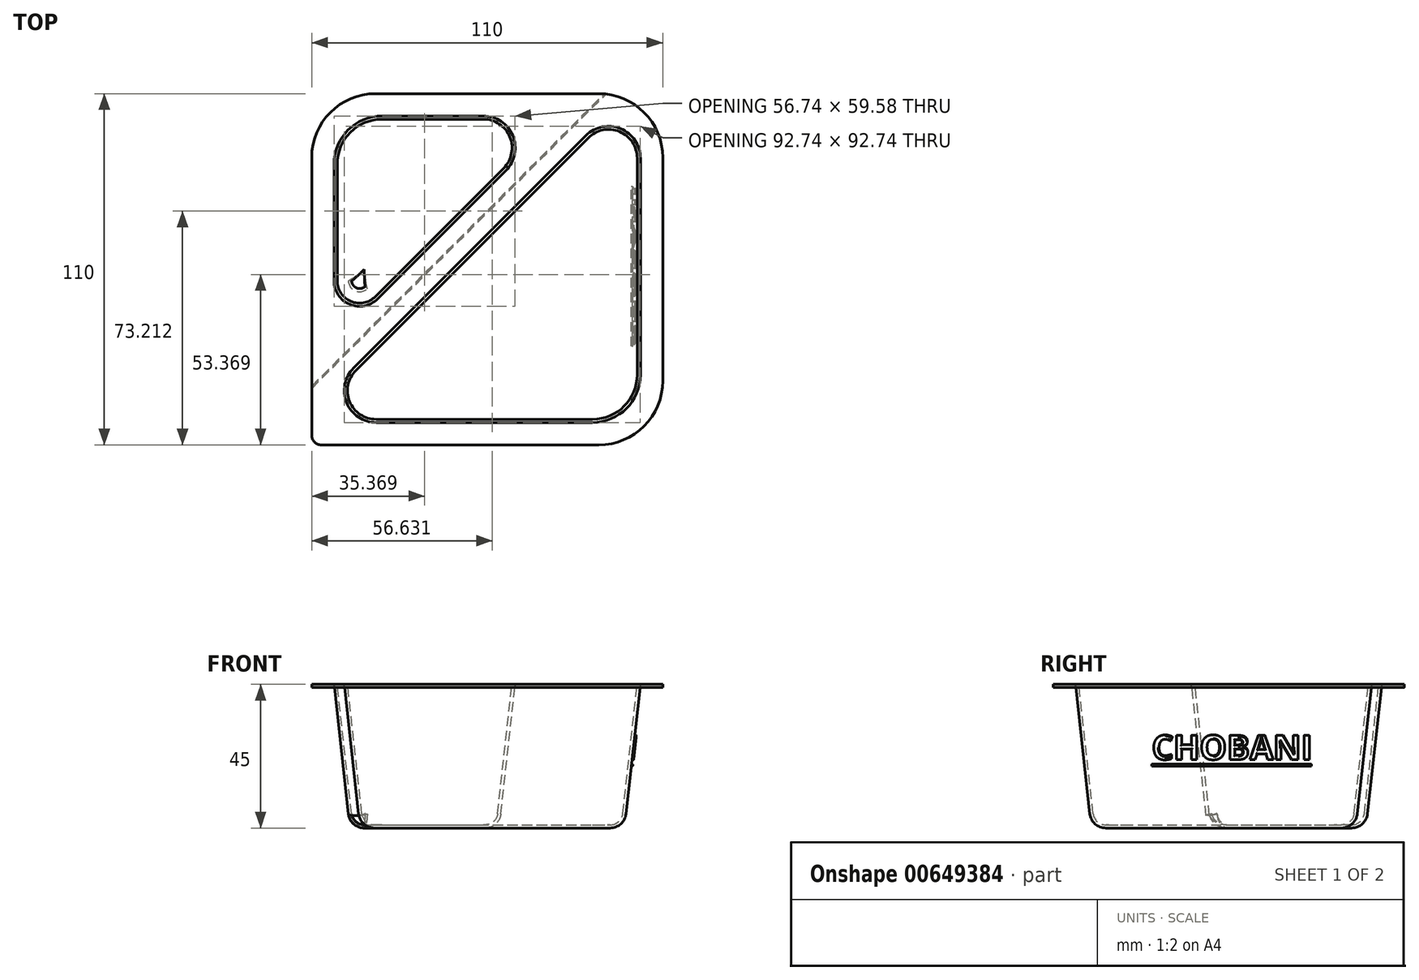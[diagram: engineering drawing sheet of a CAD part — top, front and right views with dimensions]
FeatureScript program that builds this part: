
annotation { "Feature Type Name" : "Feature", "Feature Type Description" : "" }
export const myFeature = defineFeature(function(context is Context, id is Id, definition is map)
    precondition{}
    {
        {
            var Q0;
            Q0=qCreatedBy(makeId("Top.planeOp"),FACE);
            cPlane(context, id + "F0", {"entities" : qUnion([Q0]), "cplaneType" : CPlaneType.OFFSET, "offset" : 45 * mm, "width" : 150 * mm, "height" : 150 * mm});
        }
        {
            var Q0;
            Q0=qCreatedBy(id+"F0.planeOp",FACE);
            var sketch = newSketch(context, id + "F1", { "sketchPlane" : qUnion([Q0])});
            skLineSegment(sketch, "E0.bottom", {"start": v(-52, -55) * mm, "end": v(35, -55) * mm});
            skLineSegment(sketch, "E0.top", {"start": v(-35, 55) * mm, "end": v(35, 55) * mm});
            skLineSegment(sketch, "E0.left", {"start": v(-55, -52) * mm, "end": v(-55, 35) * mm});
            skLineSegment(sketch, "E0.right", {"start": v(55, -35) * mm, "end": v(55, 35) * mm});
            skPoint(sketch, "E0.middle", {"position": v(0, 0) * mm});
            skPoint(sketch, "E1.visualSharp", {"position": v(-55, 55) * mm});
            skArc(sketch, "E1.filletArc", {"start": v(-35, 55) * mm, "mid": v(-49.14, 49.14) * mm, "end": v(-55, 35) * mm});
            skPoint(sketch, "E2.visualSharp", {"position": v(55, 55) * mm});
            skArc(sketch, "E2.filletArc", {"start": v(55, 35) * mm, "mid": v(49.14, 49.14) * mm, "end": v(35, 55) * mm});
            skPoint(sketch, "E3.visualSharp", {"position": v(55, -55) * mm});
            skArc(sketch, "E3.filletArc", {"start": v(35, -55) * mm, "mid": v(49.14, -49.14) * mm, "end": v(55, -35) * mm});
            skPoint(sketch, "E4.visualSharp", {"position": v(-55, -55) * mm});
            skArc(sketch, "E4.filletArc", {"start": v(-55, -52) * mm, "mid": v(-54.12, -54.12) * mm, "end": v(-52, -55) * mm});
            skSolve(sketch);
        }
        {
            var Q0;
            Q0=makeQuery(id+"F1.imprint","IMPRINT",FACE,{"disambiguationData":[TD([[makeQuery(id+"F1.imprint","IMPRINT",EDGE,{"derivedFrom":sQuery(id+"F1.wireOp",EDGE,"E0.bottom")}),1.0]])]});
            extrude(context, id + "F2", {"entities" : qUnion([Q0]), "oppositeDirection" : true, "depth" : 1 * mm, "offsetDistance" : 25 * mm});
        }
        {
            var Q0;
            Q0=makeQuery(id+"F2.opExtrude","CAP_FACE",FACE,{"disambiguationData":[OSD([sQuery(id+"F1.wireOp",EDGE,"E0.bottom"),sQuery(id+"F1.wireOp",EDGE,"E0.top"),sQuery(id+"F1.wireOp",EDGE,"E0.left"),sQuery(id+"F1.wireOp",EDGE,"E0.right"),sQuery(id+"F1.wireOp",EDGE,"E1.filletArc"),sQuery(id+"F1.wireOp",EDGE,"E2.filletArc"),sQuery(id+"F1.wireOp",EDGE,"E3.filletArc"),sQuery(id+"F1.wireOp",EDGE,"E4.filletArc")])],"isStart":true});
            var sketch = newSketch(context, id + "F3", { "sketchPlane" : qUnion([Q0])});
            skLineSegment(sketch, "E5", {"start": v(-55, -37) * mm, "end": v(48.56, 66.56) * mm, "construction": true});
            skLineSegment(sketch, "E6", {"start": v(-48, -3.62) * mm, "end": v(-48, 33) * mm});
            skLineSegment(sketch, "E7", {"start": v(-33, 48) * mm, "end": v(-1.21, 48) * mm});
            skLineSegment(sketch, "E8", {"start": v(5.86, 30.93) * mm, "end": v(-34.34, -9.27) * mm});
            skPoint(sketch, "E9.visualSharp", {"position": v(22.93, 48) * mm});
            skArc(sketch, "E9.filletArc", {"start": v(5.86, 30.93) * mm, "mid": v(8.03, 41.83) * mm, "end": v(-1.21, 48) * mm});
            skPoint(sketch, "E10.visualSharp", {"position": v(-48, -22.93) * mm});
            skArc(sketch, "E10.filletArc", {"start": v(-48, -3.62) * mm, "mid": v(-43.06, -11) * mm, "end": v(-34.34, -9.27) * mm});
            skPoint(sketch, "E11.visualSharp", {"position": v(-48, 48) * mm});
            skArc(sketch, "E11.filletArc", {"start": v(-33, 48) * mm, "mid": v(-43.6, 43.6) * mm, "end": v(-48, 33) * mm});
            skLineSegment(sketch, "E12", {"start": v(-34.79, -48) * mm, "end": v(33, -48) * mm});
            skLineSegment(sketch, "E13", {"start": v(48, -33) * mm, "end": v(48, 34.79) * mm});
            skLineSegment(sketch, "E14", {"start": v(30.93, 41.86) * mm, "end": v(-41.86, -30.93) * mm});
            skPoint(sketch, "E15.visualSharp", {"position": v(48, 58.93) * mm});
            skArc(sketch, "E15.filletArc", {"start": v(48, 34.79) * mm, "mid": v(41.83, 44.03) * mm, "end": v(30.93, 41.86) * mm});
            skPoint(sketch, "E16.visualSharp", {"position": v(-58.93, -48) * mm});
            skArc(sketch, "E16.filletArc", {"start": v(-41.86, -30.93) * mm, "mid": v(-44.03, -41.83) * mm, "end": v(-34.79, -48) * mm});
            skPoint(sketch, "E17.visualSharp", {"position": v(48, -48) * mm});
            skArc(sketch, "E17.filletArc", {"start": v(33, -48) * mm, "mid": v(43.6, -43.6) * mm, "end": v(48, -33) * mm});
            skSolve(sketch);
        }
        {
            var Q0;
            Q0=qCreatedBy(makeId("Top.planeOp"),FACE);
            var sketch = newSketch(context, id + "F4", { "sketchPlane" : qUnion([Q0])});
            skArc(sketch, "E18.0", {"start": v(-43, -3.62) * mm, "mid": v(-41.15, -6.39) * mm, "end": v(-37.88, -5.74) * mm});
            skArc(sketch, "E18.1", {"start": v(-33, 43) * mm, "mid": v(-40.07, 40.07) * mm, "end": v(-43, 33) * mm});
            skLineSegment(sketch, "E18.2", {"start": v(-33, 43) * mm, "end": v(-1.21, 43) * mm});
            skLineSegment(sketch, "E18.3", {"start": v(-43, -3.62) * mm, "end": v(-43, 33) * mm});
            skArc(sketch, "E18.4", {"start": v(2.32, 34.46) * mm, "mid": v(3.4, 39.91) * mm, "end": v(-1.21, 43) * mm});
            skLineSegment(sketch, "E18.5", {"start": v(2.32, 34.46) * mm, "end": v(-37.88, -5.74) * mm});
            skLineSegment(sketch, "E19.0", {"start": v(34.46, 38.32) * mm, "end": v(-38.32, -34.46) * mm});
            skLineSegment(sketch, "E19.1", {"start": v(-34.79, -43) * mm, "end": v(33, -43) * mm});
            skArc(sketch, "E19.2", {"start": v(33, -43) * mm, "mid": v(40.07, -40.07) * mm, "end": v(43, -33) * mm});
            skArc(sketch, "E19.3", {"start": v(-38.32, -34.46) * mm, "mid": v(-39.4, -39.91) * mm, "end": v(-34.79, -43) * mm});
            skLineSegment(sketch, "E19.4", {"start": v(43, -33) * mm, "end": v(43, 34.79) * mm});
            skArc(sketch, "E19.5", {"start": v(43, 34.79) * mm, "mid": v(39.91, 39.4) * mm, "end": v(34.46, 38.32) * mm});
            skSolve(sketch);
        }
        {
            var Q0;
            Q0=makeQuery(id+"F3.imprint","IMPRINT",FACE,{"disambiguationData":[TD([[makeQuery(id+"F3.imprint","IMPRINT",EDGE,{"derivedFrom":sQuery(id+"F3.wireOp",EDGE,"E6")}),-1.0]])]});
            var Q1;
            Q1=makeQuery(id+"F3.imprint","IMPRINT",FACE,{"disambiguationData":[TD([[makeQuery(id+"F3.imprint","IMPRINT",EDGE,{"derivedFrom":sQuery(id+"F3.wireOp",EDGE,"E12")}),1.0]])]});
            extrude(context, id + "F5", {"entities" : qUnion([Q0, Q1]), "operationType" : NewBodyOperationType.REMOVE, "oppositeDirection" : true, "depth" : 25 * mm, "offsetDistance" : 25 * mm});
        }
        {
            var Q0;
            Q0=makeQuery(id+"F3.imprint","IMPRINT",FACE,{"disambiguationData":[TD([[makeQuery(id+"F3.imprint","IMPRINT",EDGE,{"derivedFrom":sQuery(id+"F3.wireOp",EDGE,"E6")}),-1.0]])]});
            var Q1;
            Q1=makeQuery(id+"F4.imprint","IMPRINT",FACE,{"disambiguationData":[TD([[makeQuery(id+"F4.imprint","IMPRINT",EDGE,{"derivedFrom":sQuery(id+"F4.wireOp",EDGE,"E18.0")}),1.0]])]});
            loft(context, id + "F6", {"sheetProfilesArray" : [{ "sheetProfileEntities" : qUnion([Q0]) }, { "sheetProfileEntities" : qUnion([Q1]) }]});
        }
        {
            var Q0;
            Q0=makeQuery(id+"F3.imprint","IMPRINT",FACE,{"disambiguationData":[TD([[makeQuery(id+"F3.imprint","IMPRINT",EDGE,{"derivedFrom":sQuery(id+"F3.wireOp",EDGE,"E12")}),1.0]])]});
            var Q1;
            Q1=makeQuery(id+"F4.imprint","IMPRINT",FACE,{"disambiguationData":[TD([[makeQuery(id+"F4.imprint","IMPRINT",EDGE,{"derivedFrom":sQuery(id+"F4.wireOp",EDGE,"E19.0")}),1.0]])]});
            loft(context, id + "F7", {"sheetProfilesArray" : [{ "sheetProfileEntities" : qUnion([Q0]) }, { "sheetProfileEntities" : qUnion([Q1]) }]});
        }
        {
            var Q0;
            Q0=makeQuery(id+"F6.opLoft","MID_CAP_EDGE",EDGE,{"disambiguationData":[OSD([sQuery(id+"F4.wireOp",EDGE,"E18.1"),sQuery(id+"F4.wireOp",EDGE,"E18.2"),sQuery(id+"F4.wireOp",EDGE,"E18.3")])],"capPos":1.0});
            fillet(context, id + "F8", {"entities" : qUnion([Q0]), "radius" : 5 * mm, "tangentPropagation" : true, "allowEdgeOverflow" : false});
        }
        {
            var Q0;
            Q0=makeQuery(id+"F6.opLoft","CAP_FACE",FACE,{"disambiguationData":[OSD([makeQuery(id+"F3.imprint","IMPRINT",FACE,{"disambiguationData":[TD([[makeQuery(id+"F3.imprint","IMPRINT",EDGE,{"derivedFrom":sQuery(id+"F3.wireOp",EDGE,"E6")}),-1.0]])]})])],"isStart":true});
            shell(context, id + "F9", {"entities" : qUnion([Q0]), "thickness" : 1 * mm});
        }
        {
            var Q0;
            Q0=makeQuery(id+"F7.opLoft","MID_CAP_EDGE",EDGE,{"disambiguationData":[OSD([sQuery(id+"F4.wireOp",EDGE,"E19.0"),sQuery(id+"F4.wireOp",EDGE,"E19.1"),sQuery(id+"F4.wireOp",EDGE,"E19.3")])],"capPos":1.0});
            fillet(context, id + "F10", {"entities" : qUnion([Q0]), "radius" : 5 * mm, "tangentPropagation" : true, "allowEdgeOverflow" : false});
        }
        {
            var Q0;
            Q0=makeQuery(id+"F7.opLoft","CAP_FACE",FACE,{"disambiguationData":[OSD([makeQuery(id+"F3.imprint","IMPRINT",FACE,{"disambiguationData":[TD([[makeQuery(id+"F3.imprint","IMPRINT",EDGE,{"derivedFrom":sQuery(id+"F3.wireOp",EDGE,"E12")}),1.0]])]})])],"isStart":true});
            shell(context, id + "F11", {"entities" : qUnion([Q0]), "thickness" : 1 * mm});
        }
        {
            var Q0;
            Q0=sQuery(id+"F3.wireOp",VERTEX,"E5.end");
            var Q1;
            Q1=sQuery(id+"F3.wireOp",EDGE,"E5");
            cPlane(context, id + "F12", {"entities" : qUnion([Q0, Q1]), "cplaneType" : CPlaneType.LINE_POINT, "offset" : 25 * mm, "width" : 150 * mm, "height" : 150 * mm});
        }
        {
            var Q0;
            Q0=qCreatedBy(id+"F12.planeOp",FACE);
            var sketch = newSketch(context, id + "F13", { "sketchPlane" : qUnion([Q0])});
            skLineSegment(sketch, "E20", {"start": v(12.73, 44.3) * mm, "end": v(12.98, 44) * mm});
            skLineSegment(sketch, "E21", {"start": v(12.98, 44) * mm, "end": v(12.48, 44) * mm});
            skLineSegment(sketch, "E22", {"start": v(12.48, 44) * mm, "end": v(12.73, 44.3) * mm});
            skSolve(sketch);
        }
        {
            var Q0;
            Q0=makeQuery(id+"F13.imprint","IMPRINT",FACE,{"disambiguationData":[TD([[makeQuery(id+"F13.imprint","IMPRINT",EDGE,{"derivedFrom":sQuery(id+"F13.wireOp",EDGE,"E20")}),-1.0]])]});
            extrude(context, id + "F14", {"entities" : qUnion([Q0]), "operationType" : NewBodyOperationType.REMOVE, "endBound" : BoundingType.THROUGH_ALL, "oppositeDirection" : true, "depth" : 25 * mm, "offsetDistance" : 25 * mm});
        }
        {
            var Q0;
            Q0=makeQuery(id+"F7.opLoft","SWEPT_FACE",FACE,{"disambiguationData":[OSD([sQuery(id+"F3.wireOp",EDGE,"E13"),sQuery(id+"F3.wireOp",EDGE,"E15.filletArc"),sQuery(id+"F3.wireOp",EDGE,"E17.filletArc"),sQuery(id+"F4.wireOp",EDGE,"E19.2"),sQuery(id+"F4.wireOp",EDGE,"E19.4"),sQuery(id+"F4.wireOp",EDGE,"E19.5")])]});
            var sketch = newSketch(context, id + "F15", { "sketchPlane" : qUnion([Q0])});
            skText(sketch, "E23", { "text": "CHOBANI", "fontName": "OpenSans-Bold.ttf"});
            skLineSegment(sketch, "E24.bottom", {"start": v(-24.1, 24.84) * mm, "end": v(25.9, 24.84) * mm});
            skLineSegment(sketch, "E24.top", {"start": v(-24.1, 24.34) * mm, "end": v(25.9, 24.34) * mm});
            skLineSegment(sketch, "E24.left", {"start": v(-24.1, 24.84) * mm, "end": v(-24.1, 24.34) * mm});
            skLineSegment(sketch, "E24.right", {"start": v(25.9, 24.84) * mm, "end": v(25.9, 24.34) * mm});
            const initialGuessF15  = {"E23": [-0.0241, 0.02634, 1, 0, 0.0077]};
            skSetInitialGuess(sketch, initialGuessF15);
            skSolve(sketch);
        }
        {
            var Q0;
            Q0 = qSketchRegion(id + "F15", true);
            extrude(context, id + "F16", {"entities" : qUnion([Q0]), "operationType" : NewBodyOperationType.ADD, "depth" : .5 * mm, "offsetDistance" : 25 * mm});
        }
        {
            var Q0;
            Q0=makeQuery(id+"F16.opExtrude","CAP_FACE",FACE,{"disambiguationData":[OSD([sQuery(id+"F15.wireOp",EDGE,"E23.sketch_text.stroke-0"),sQuery(id+"F15.wireOp",EDGE,"E23.sketch_text.stroke-1"),sQuery(id+"F15.wireOp",EDGE,"E23.sketch_text.stroke-2"),sQuery(id+"F15.wireOp",EDGE,"E23.sketch_text.stroke-3"),sQuery(id+"F15.wireOp",EDGE,"E23.sketch_text.stroke-4"),sQuery(id+"F15.wireOp",EDGE,"E23.sketch_text.stroke-5"),sQuery(id+"F15.wireOp",EDGE,"E23.sketch_text.stroke-6"),sQuery(id+"F15.wireOp",EDGE,"E23.sketch_text.stroke-7"),sQuery(id+"F15.wireOp",EDGE,"E23.sketch_text.stroke-8"),sQuery(id+"F15.wireOp",EDGE,"E23.sketch_text.stroke-9"),sQuery(id+"F15.wireOp",EDGE,"E23.sketch_text.stroke-10"),sQuery(id+"F15.wireOp",EDGE,"E23.sketch_text.stroke-11"),sQuery(id+"F15.wireOp",EDGE,"E23.sketch_text.stroke-12"),sQuery(id+"F15.wireOp",EDGE,"E23.sketch_text.stroke-13"),sQuery(id+"F15.wireOp",EDGE,"E23.sketch_text.stroke-14")])],"isStart":false});
            var Q1;
            Q1=makeQuery(id+"F16.opExtrude","CAP_FACE",FACE,{"disambiguationData":[OSD([sQuery(id+"F15.wireOp",EDGE,"E23.sketch_text.stroke-15"),sQuery(id+"F15.wireOp",EDGE,"E23.sketch_text.stroke-16"),sQuery(id+"F15.wireOp",EDGE,"E23.sketch_text.stroke-17"),sQuery(id+"F15.wireOp",EDGE,"E23.sketch_text.stroke-18"),sQuery(id+"F15.wireOp",EDGE,"E23.sketch_text.stroke-19"),sQuery(id+"F15.wireOp",EDGE,"E23.sketch_text.stroke-20"),sQuery(id+"F15.wireOp",EDGE,"E23.sketch_text.stroke-21"),sQuery(id+"F15.wireOp",EDGE,"E23.sketch_text.stroke-22"),sQuery(id+"F15.wireOp",EDGE,"E23.sketch_text.stroke-23"),sQuery(id+"F15.wireOp",EDGE,"E23.sketch_text.stroke-24"),sQuery(id+"F15.wireOp",EDGE,"E23.sketch_text.stroke-25"),sQuery(id+"F15.wireOp",EDGE,"E23.sketch_text.stroke-26")])],"isStart":false});
            var Q2;
            Q2=makeQuery(id+"F16.opExtrude","CAP_FACE",FACE,{"disambiguationData":[OSD([sQuery(id+"F15.wireOp",EDGE,"E23.sketch_text.stroke-27"),sQuery(id+"F15.wireOp",EDGE,"E23.sketch_text.stroke-28"),sQuery(id+"F15.wireOp",EDGE,"E23.sketch_text.stroke-29"),sQuery(id+"F15.wireOp",EDGE,"E23.sketch_text.stroke-30"),sQuery(id+"F15.wireOp",EDGE,"E23.sketch_text.stroke-31"),sQuery(id+"F15.wireOp",EDGE,"E23.sketch_text.stroke-32"),sQuery(id+"F15.wireOp",EDGE,"E23.sketch_text.stroke-33"),sQuery(id+"F15.wireOp",EDGE,"E23.sketch_text.stroke-34"),sQuery(id+"F15.wireOp",EDGE,"E23.sketch_text.stroke-35"),sQuery(id+"F15.wireOp",EDGE,"E23.sketch_text.stroke-36"),sQuery(id+"F15.wireOp",EDGE,"E23.sketch_text.stroke-37"),sQuery(id+"F15.wireOp",EDGE,"E23.sketch_text.stroke-38"),sQuery(id+"F15.wireOp",EDGE,"E23.sketch_text.stroke-39"),sQuery(id+"F15.wireOp",EDGE,"E23.sketch_text.stroke-40")])],"isStart":false});
            var Q3;
            Q3=makeQuery(id+"F16.opExtrude","CAP_FACE",FACE,{"disambiguationData":[OSD([sQuery(id+"F15.wireOp",EDGE,"E23.sketch_text.stroke-41"),sQuery(id+"F15.wireOp",EDGE,"E23.sketch_text.stroke-42"),sQuery(id+"F15.wireOp",EDGE,"E23.sketch_text.stroke-43"),sQuery(id+"F15.wireOp",EDGE,"E23.sketch_text.stroke-44"),sQuery(id+"F15.wireOp",EDGE,"E23.sketch_text.stroke-45"),sQuery(id+"F15.wireOp",EDGE,"E23.sketch_text.stroke-46"),sQuery(id+"F15.wireOp",EDGE,"E23.sketch_text.stroke-47"),sQuery(id+"F15.wireOp",EDGE,"E23.sketch_text.stroke-48"),sQuery(id+"F15.wireOp",EDGE,"E23.sketch_text.stroke-49"),sQuery(id+"F15.wireOp",EDGE,"E23.sketch_text.stroke-50"),sQuery(id+"F15.wireOp",EDGE,"E23.sketch_text.stroke-51"),sQuery(id+"F15.wireOp",EDGE,"E23.sketch_text.stroke-52"),sQuery(id+"F15.wireOp",EDGE,"E23.sketch_text.stroke-53"),sQuery(id+"F15.wireOp",EDGE,"E23.sketch_text.stroke-54"),sQuery(id+"F15.wireOp",EDGE,"E23.sketch_text.stroke-55"),sQuery(id+"F15.wireOp",EDGE,"E23.sketch_text.stroke-56"),sQuery(id+"F15.wireOp",EDGE,"E23.sketch_text.stroke-57"),sQuery(id+"F15.wireOp",EDGE,"E23.sketch_text.stroke-58"),sQuery(id+"F15.wireOp",EDGE,"E23.sketch_text.stroke-59"),sQuery(id+"F15.wireOp",EDGE,"E23.sketch_text.stroke-60"),sQuery(id+"F15.wireOp",EDGE,"E23.sketch_text.stroke-61"),sQuery(id+"F15.wireOp",EDGE,"E23.sketch_text.stroke-62"),sQuery(id+"F15.wireOp",EDGE,"E23.sketch_text.stroke-63"),sQuery(id+"F15.wireOp",EDGE,"E23.sketch_text.stroke-64"),sQuery(id+"F15.wireOp",EDGE,"E23.sketch_text.stroke-65")])],"isStart":false});
            var Q4;
            Q4=makeQuery(id+"F16.opExtrude","CAP_FACE",FACE,{"disambiguationData":[OSD([sQuery(id+"F15.wireOp",EDGE,"E23.sketch_text.stroke-66"),sQuery(id+"F15.wireOp",EDGE,"E23.sketch_text.stroke-67"),sQuery(id+"F15.wireOp",EDGE,"E23.sketch_text.stroke-68"),sQuery(id+"F15.wireOp",EDGE,"E23.sketch_text.stroke-69"),sQuery(id+"F15.wireOp",EDGE,"E23.sketch_text.stroke-70"),sQuery(id+"F15.wireOp",EDGE,"E23.sketch_text.stroke-71"),sQuery(id+"F15.wireOp",EDGE,"E23.sketch_text.stroke-72"),sQuery(id+"F15.wireOp",EDGE,"E23.sketch_text.stroke-73"),sQuery(id+"F15.wireOp",EDGE,"E23.sketch_text.stroke-74"),sQuery(id+"F15.wireOp",EDGE,"E23.sketch_text.stroke-75"),sQuery(id+"F15.wireOp",EDGE,"E23.sketch_text.stroke-76"),sQuery(id+"F15.wireOp",EDGE,"E23.sketch_text.stroke-77")])],"isStart":false});
            var Q5;
            Q5=makeQuery(id+"F16.opExtrude","CAP_FACE",FACE,{"disambiguationData":[OSD([sQuery(id+"F15.wireOp",EDGE,"E23.sketch_text.stroke-78"),sQuery(id+"F15.wireOp",EDGE,"E23.sketch_text.stroke-79"),sQuery(id+"F15.wireOp",EDGE,"E23.sketch_text.stroke-80"),sQuery(id+"F15.wireOp",EDGE,"E23.sketch_text.stroke-81"),sQuery(id+"F15.wireOp",EDGE,"E23.sketch_text.stroke-82"),sQuery(id+"F15.wireOp",EDGE,"E23.sketch_text.stroke-83"),sQuery(id+"F15.wireOp",EDGE,"E23.sketch_text.stroke-84"),sQuery(id+"F15.wireOp",EDGE,"E23.sketch_text.stroke-85"),sQuery(id+"F15.wireOp",EDGE,"E23.sketch_text.stroke-86"),sQuery(id+"F15.wireOp",EDGE,"E23.sketch_text.stroke-87"),sQuery(id+"F15.wireOp",EDGE,"E23.sketch_text.stroke-88"),sQuery(id+"F15.wireOp",EDGE,"E23.sketch_text.stroke-89"),sQuery(id+"F15.wireOp",EDGE,"E23.sketch_text.stroke-90"),sQuery(id+"F15.wireOp",EDGE,"E23.sketch_text.stroke-91")])],"isStart":false});
            var Q6;
            Q6=makeQuery(id+"F16.opExtrude","CAP_FACE",FACE,{"disambiguationData":[OSD([sQuery(id+"F15.wireOp",EDGE,"E23.sketch_text.stroke-92"),sQuery(id+"F15.wireOp",EDGE,"E23.sketch_text.stroke-93"),sQuery(id+"F15.wireOp",EDGE,"E23.sketch_text.stroke-94"),sQuery(id+"F15.wireOp",EDGE,"E23.sketch_text.stroke-95")])],"isStart":false});
            var Q7;
            Q7=makeQuery(id+"F16.opExtrude","CAP_FACE",FACE,{"disambiguationData":[OSD([sQuery(id+"F15.wireOp",EDGE,"E24.bottom"),sQuery(id+"F15.wireOp",EDGE,"E24.top"),sQuery(id+"F15.wireOp",EDGE,"E24.left"),sQuery(id+"F15.wireOp",EDGE,"E24.right")])],"isStart":false});
            fillet(context, id + "F17", {"entities" : qUnion([Q0, Q1, Q2, Q3, Q4, Q5, Q6, Q7]), "radius" : .25 * mm, "tangentPropagation" : true, "allowEdgeOverflow" : false});
        }
    });
